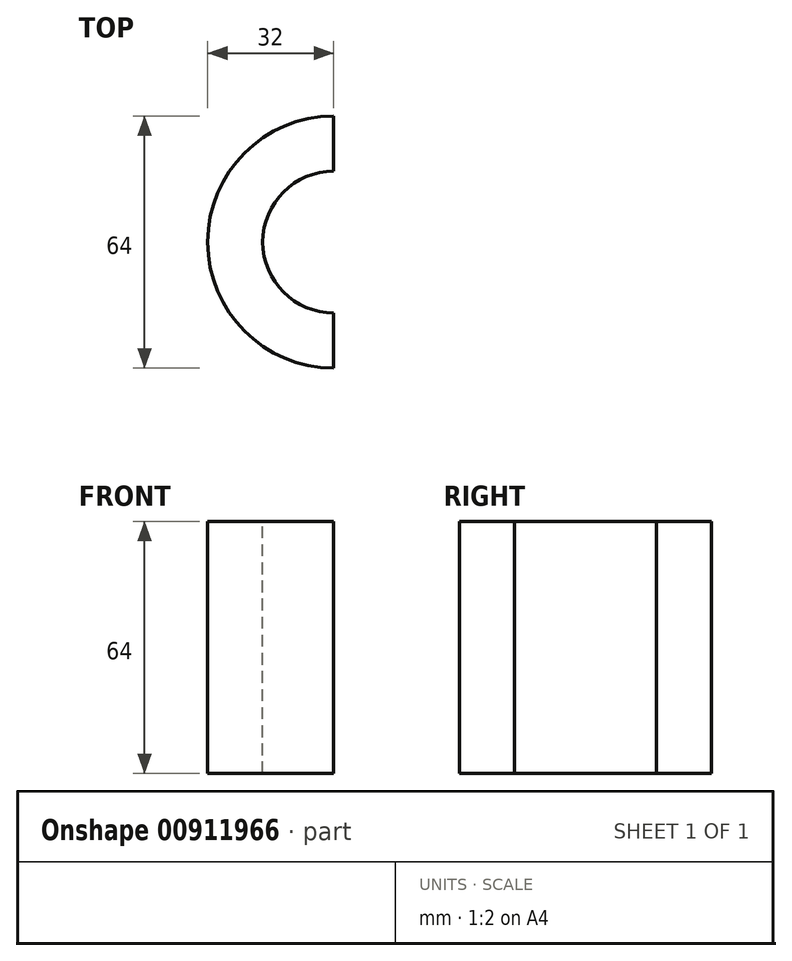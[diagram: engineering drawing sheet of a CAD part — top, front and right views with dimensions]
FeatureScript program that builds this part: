
annotation { "Feature Type Name" : "Feature", "Feature Type Description" : "" }
export const myFeature = defineFeature(function(context is Context, id is Id, definition is map)
    precondition{}
    {
        {
            var Q0;
            Q0=qCreatedBy(makeId("Top.planeOp"),FACE);
            var sketch = newSketch(context, id + "F0", { "sketchPlane" : qUnion([Q0])});
            skArc(sketch, "E0", {"start": v(0, 32) * mm, "mid": v(-32, 0) * mm, "end": v(0, -32) * mm});
            skArc(sketch, "E1", {"start": v(0, 18) * mm, "mid": v(-18, 0) * mm, "end": v(0, -18) * mm});
            skLineSegment(sketch, "E2", {"start": v(0, 32) * mm, "end": v(0, 18) * mm});
            skLineSegment(sketch, "E3", {"start": v(0, -18) * mm, "end": v(0, -32) * mm});
            skSolve(sketch);
        }
        {
            var Q0;
            Q0=makeQuery(id+"F0.imprint","IMPRINT",FACE,{"disambiguationData":[TD([[makeQuery(id+"F0.imprint","IMPRINT",EDGE,{"derivedFrom":sQuery(id+"F0.wireOp",EDGE,"E0")}),1.0]])]});
            extrude(context, id + "F1", {"entities" : qUnion([Q0]), "oppositeDirection" : true, "depth" : 64 * mm, "offsetDistance" : 25 * mm});
        }
    });
